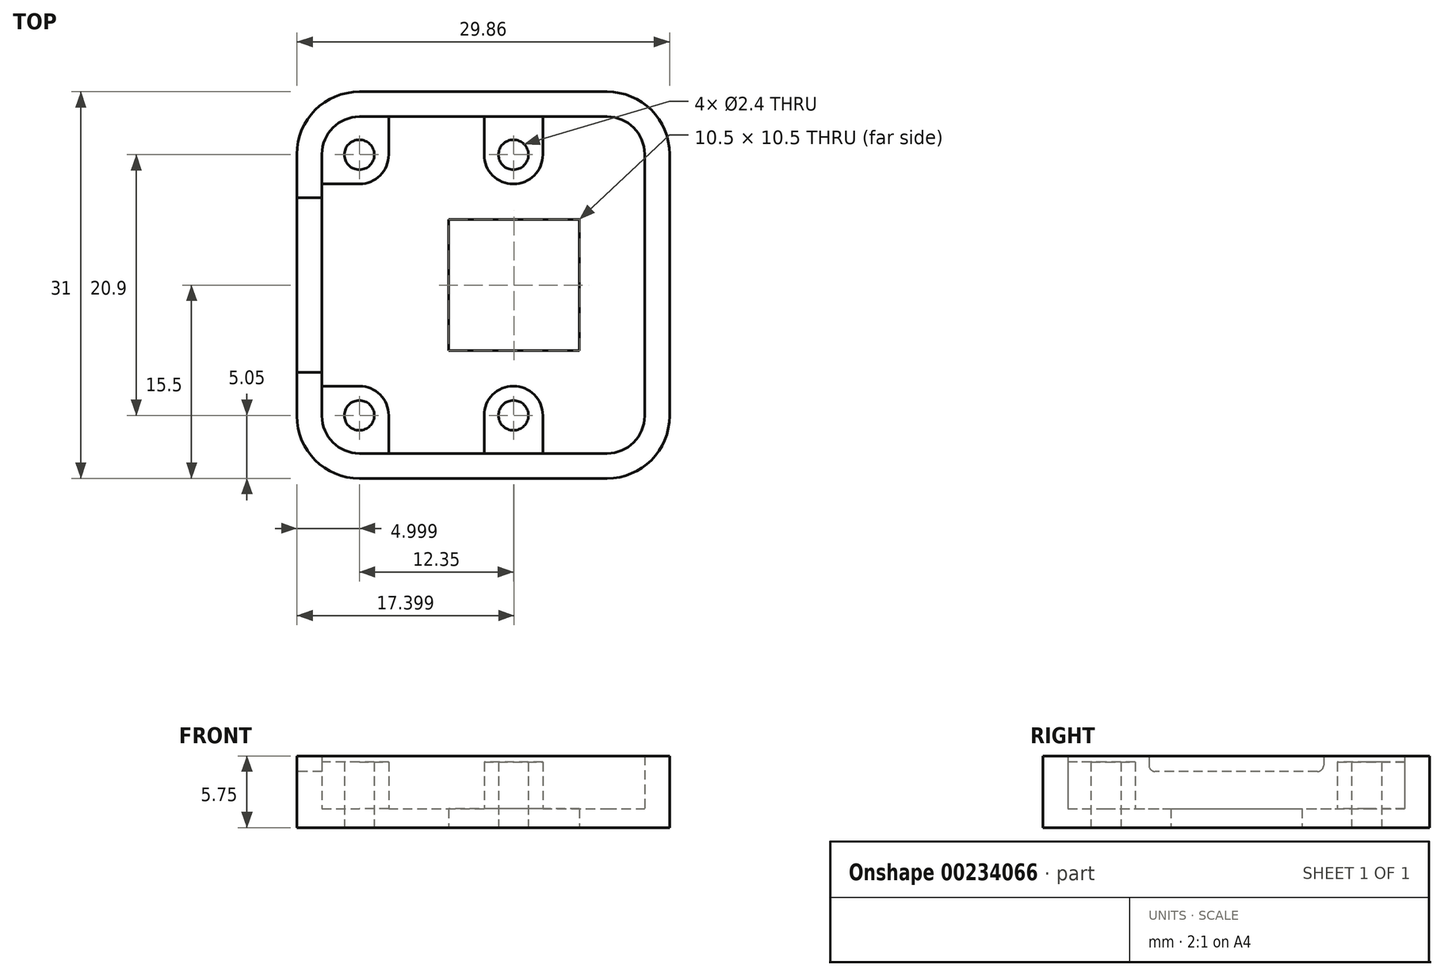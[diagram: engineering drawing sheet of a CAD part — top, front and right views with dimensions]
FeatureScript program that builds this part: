
annotation { "Feature Type Name" : "Feature", "Feature Type Description" : "" }
export const myFeature = defineFeature(function(context is Context, id is Id, definition is map)
    precondition{}
    {
        {
            var Q0;
            Q0=qCreatedBy(makeId("Top.planeOp"),FACE);
            var sketch = newSketch(context, id + "F0", { "sketchPlane" : qUnion([Q0])});
            skPoint(sketch, "E0.middle", {"position": v(0, 0) * mm});
            skPoint(sketch, "E1.visualSharp", {"position": v(-11.93, 12.5) * mm});
            skPoint(sketch, "E2.visualSharp", {"position": v(-11.93, -12.5) * mm});
            skPoint(sketch, "E3.visualSharp", {"position": v(11.93, 12.5) * mm});
            skPoint(sketch, "E4.visualSharp", {"position": v(11.93, -12.5) * mm});
            skLineSegment(sketch, "E5", {"start": v(-9.93, 14.98) * mm, "end": v(-9.93, -15.05) * mm, "construction": true});
            skLineSegment(sketch, "E6", {"start": v(-20.4, -10.45) * mm, "end": v(21.47, -10.45) * mm, "construction": true});
            skLineSegment(sketch, "E7", {"start": v(-14.71, 10.45) * mm, "end": v(19.25, 10.45) * mm, "construction": true});
            skCircle(sketch, "E8", {"center": v(-9.93, 10.45) * mm, "radius": 1.2 * mm});
            skCircle(sketch, "E9", {"center": v(-9.93, -10.45) * mm, "radius": 1.2 * mm});
            skLineSegment(sketch, "E10", {"start": v(2.42, 14.76) * mm, "end": v(2.42, -15.1) * mm, "construction": true});
            skCircle(sketch, "E11", {"center": v(2.42, 10.45) * mm, "radius": 1.2 * mm});
            skCircle(sketch, "E12", {"center": v(2.42, -10.45) * mm, "radius": 1.2 * mm});
            skLineSegment(sketch, "E13", {"start": v(2.47, 15.16) * mm, "end": v(2.47, -14.75) * mm, "construction": true});
            skLineSegment(sketch, "E14.bottom", {"start": v(6.72, -4.25) * mm, "end": v(-1.78, -4.25) * mm});
            skLineSegment(sketch, "E14.top", {"start": v(6.72, 4.25) * mm, "end": v(-1.78, 4.25) * mm});
            skLineSegment(sketch, "E14.left", {"start": v(6.72, -4.25) * mm, "end": v(6.72, 4.25) * mm});
            skLineSegment(sketch, "E14.right", {"start": v(-1.78, -4.25) * mm, "end": v(-1.78, 4.25) * mm});
            skPoint(sketch, "E14.middle", {"position": v(2.47, 0) * mm});
            skCircle(sketch, "E15", {"center": v(-9.93, 10.45) * mm, "radius": 2.35 * mm});
            skCircle(sketch, "E16", {"center": v(-9.93, -10.45) * mm, "radius": 2.35 * mm});
            skCircle(sketch, "E17", {"center": v(2.42, -10.45) * mm, "radius": 2.35 * mm});
            skCircle(sketch, "E18", {"center": v(2.42, 10.45) * mm, "radius": 2.35 * mm});
            skLineSegment(sketch, "E19.0", {"start": v(7.72, 5.25) * mm, "end": v(-2.78, 5.25) * mm});
            skLineSegment(sketch, "E19.1", {"start": v(7.72, -5.25) * mm, "end": v(7.72, 5.25) * mm});
            skLineSegment(sketch, "E19.2", {"start": v(7.72, -5.25) * mm, "end": v(-2.78, -5.25) * mm});
            skLineSegment(sketch, "E19.3", {"start": v(-2.78, -5.25) * mm, "end": v(-2.78, 5.25) * mm});
            skLineSegment(sketch, "E20.0", {"start": v(9.93, 13.5) * mm, "end": v(-9.93, 13.5) * mm});
            skArc(sketch, "E20.1", {"start": v(12.93, 10.5) * mm, "mid": v(12.05, 12.62) * mm, "end": v(9.93, 13.5) * mm});
            skArc(sketch, "E20.2", {"start": v(-9.93, 13.5) * mm, "mid": v(-12.05, 12.62) * mm, "end": v(-12.93, 10.5) * mm});
            skLineSegment(sketch, "E20.3", {"start": v(12.93, 10.5) * mm, "end": v(12.93, -10.5) * mm});
            skLineSegment(sketch, "E20.4", {"start": v(-12.93, 10.5) * mm, "end": v(-12.93, -10.5) * mm});
            skArc(sketch, "E20.5", {"start": v(-12.93, -10.5) * mm, "mid": v(-12.05, -12.62) * mm, "end": v(-9.93, -13.5) * mm});
            skLineSegment(sketch, "E20.6", {"start": v(9.93, -13.5) * mm, "end": v(-9.93, -13.5) * mm});
            skArc(sketch, "E20.7", {"start": v(9.93, -13.5) * mm, "mid": v(12.05, -12.62) * mm, "end": v(12.93, -10.5) * mm});
            skArc(sketch, "E21.0", {"start": v(14.93, 10.5) * mm, "mid": v(13.47, 14.04) * mm, "end": v(9.93, 15.5) * mm});
            skLineSegment(sketch, "E21.1", {"start": v(14.93, 10.5) * mm, "end": v(14.93, -10.5) * mm});
            skLineSegment(sketch, "E21.2", {"start": v(9.93, 15.5) * mm, "end": v(-9.93, 15.5) * mm});
            skArc(sketch, "E21.3", {"start": v(9.93, -15.5) * mm, "mid": v(13.47, -14.04) * mm, "end": v(14.93, -10.5) * mm});
            skArc(sketch, "E21.4", {"start": v(-9.93, 15.5) * mm, "mid": v(-13.47, 14.04) * mm, "end": v(-14.93, 10.5) * mm});
            skLineSegment(sketch, "E21.5", {"start": v(-14.93, 10.5) * mm, "end": v(-14.93, -10.5) * mm});
            skArc(sketch, "E21.6", {"start": v(-14.93, -10.5) * mm, "mid": v(-13.47, -14.04) * mm, "end": v(-9.93, -15.5) * mm});
            skLineSegment(sketch, "E21.7", {"start": v(9.93, -15.5) * mm, "end": v(-9.93, -15.5) * mm});
            skLineSegment(sketch, "E22", {"start": v(-9.93, 8.1) * mm, "end": v(-12.93, 8.1) * mm});
            skLineSegment(sketch, "E23", {"start": v(-7.58, 10.45) * mm, "end": v(-7.58, 13.5) * mm});
            skLineSegment(sketch, "E24", {"start": v(0.07, 10.45) * mm, "end": v(0.07, 13.5) * mm});
            skLineSegment(sketch, "E25", {"start": v(4.77, 10.45) * mm, "end": v(4.77, 13.5) * mm});
            skLineSegment(sketch, "E26", {"start": v(0.07, -10.45) * mm, "end": v(0.07, -13.5) * mm});
            skLineSegment(sketch, "E27", {"start": v(4.77, -10.45) * mm, "end": v(4.77, -13.5) * mm});
            skLineSegment(sketch, "E28", {"start": v(-9.93, -8.1) * mm, "end": v(-12.93, -8.1) * mm});
            skLineSegment(sketch, "E29", {"start": v(-7.58, -10.45) * mm, "end": v(-7.58, -13.5) * mm});
            skSolve(sketch);
        }
        {
            var Q0;
            Q0=makeQuery(id+"F0.imprint","IMPRINT",FACE,{"disambiguationData":[TD([[makeQuery(id+"F0.imprint","IMPRINT",EDGE,{"derivedFrom":sQuery(id+"F0.wireOp",EDGE,"E20.0")}),-1.0]])]});
            var Q1;
            Q1=makeQuery(id+"F0.imprint","IMPRINT",FACE,{"disambiguationData":[TD([[makeQuery(id+"F0.imprint","IMPRINT",EDGE,{"derivedFrom":sQuery(id+"F0.wireOp",EDGE,"E0.left")}),-1.0]])]});
            var Q2;
            Q2=makeQuery(id+"F0.imprint","IMPRINT",FACE,{"disambiguationData":[TD([[makeQuery(id+"F0.imprint","IMPRINT",EDGE,{"derivedFrom":sQuery(id+"F0.wireOp",EDGE,"E12")}),-1.0]])]});
            var Q3;
            {var subQ0=sQuery(id+"F0.wireOp",EDGE,"E2.filletArc");Q3=makeQuery(id+"F0.imprint","IMPRINT",FACE,{"disambiguationData":[TD([[makeQuery(id+"F0.imprint","IMPRINT",EDGE,{"derivedFrom":subQ0}),1.0]])]});}
            var Q4;
            Q4=makeQuery(id+"F0.imprint","IMPRINT",FACE,{"disambiguationData":[TD([[makeQuery(id+"F0.imprint","IMPRINT",EDGE,{"derivedFrom":sQuery(id+"F0.wireOp",EDGE,"E0.left")}),1.0]])]});
            var Q5;
            {var subQ0=sQuery(id+"F0.wireOp",EDGE,"E1.filletArc");Q5=makeQuery(id+"F0.imprint","IMPRINT",FACE,{"disambiguationData":[TD([[makeQuery(id+"F0.imprint","IMPRINT",EDGE,{"derivedFrom":subQ0}),1.0]])]});}
            var Q6;
            Q6=makeQuery(id+"F0.imprint","IMPRINT",FACE,{"disambiguationData":[TD([[makeQuery(id+"F0.imprint","IMPRINT",EDGE,{"derivedFrom":sQuery(id+"F0.wireOp",EDGE,"E11")}),-1.0]])]});
            var Q7;
            {var subQ0=sQuery(id+"F0.wireOp",EDGE,"E18");var subQ1=sQuery(id+"F0.wireOp",EDGE,"E0.bottom");var subQ2=makeQuery(id+"F0.imprint","INTERSECT",VERTEX,{"disambiguationData":[OD(0.0)],"derivedFrom":[subQ1,subQ0]});Q7=makeQuery(id+"F0.imprint","IMPRINT",FACE,{"disambiguationData":[TD([[makeQuery(id+"F0.imprint","IMPRINT",EDGE,{"disambiguationData":[TD([[subQ2,-1.0]])],"derivedFrom":subQ1}),-1.0]])]});}
            var Q8;
            {var subQ0=sQuery(id+"F0.wireOp",EDGE,"E1.filletArc");Q8=makeQuery(id+"F0.imprint","IMPRINT",FACE,{"disambiguationData":[TD([[makeQuery(id+"F0.imprint","IMPRINT",EDGE,{"derivedFrom":subQ0}),-1.0]])]});}
            var Q9;
            {var subQ0=sQuery(id+"F0.wireOp",EDGE,"E2.filletArc");Q9=makeQuery(id+"F0.imprint","IMPRINT",FACE,{"disambiguationData":[TD([[makeQuery(id+"F0.imprint","IMPRINT",EDGE,{"derivedFrom":subQ0}),-1.0]])]});}
            var Q10;
            {var subQ0=sQuery(id+"F0.wireOp",EDGE,"E17");var subQ1=sQuery(id+"F0.wireOp",EDGE,"E0.top");var subQ2=makeQuery(id+"F0.imprint","INTERSECT",VERTEX,{"disambiguationData":[OD(0.0)],"derivedFrom":[subQ1,subQ0]});Q10=makeQuery(id+"F0.imprint","IMPRINT",FACE,{"disambiguationData":[TD([[makeQuery(id+"F0.imprint","IMPRINT",EDGE,{"disambiguationData":[TD([[subQ2,-1.0]])],"derivedFrom":subQ1}),1.0]])]});}
            var Q11;
            {var subQ0=sQuery(id+"F0.wireOp",EDGE,"E20.2");Q11=makeQuery(id+"F0.imprint","IMPRINT",FACE,{"disambiguationData":[TD([[makeQuery(id+"F0.imprint","IMPRINT",EDGE,{"derivedFrom":subQ0}),1.0]])]});}
            var Q12;
            {var subQ0=sQuery(id+"F0.wireOp",EDGE,"E22");var subQ1=sQuery(id+"F0.wireOp",EDGE,"E0.right");var subQ2=makeQuery(id+"F0.imprint","INTERSECT",VERTEX,{"derivedFrom":[subQ1,subQ0]});Q12=makeQuery(id+"F0.imprint","IMPRINT",FACE,{"disambiguationData":[TD([[makeQuery(id+"F0.imprint","IMPRINT",EDGE,{"disambiguationData":[TD([[subQ2,-1.0]])],"derivedFrom":subQ1}),-1.0]])]});}
            var Q13;
            {var subQ0=sQuery(id+"F0.wireOp",EDGE,"E20.5");Q13=makeQuery(id+"F0.imprint","IMPRINT",FACE,{"disambiguationData":[TD([[makeQuery(id+"F0.imprint","IMPRINT",EDGE,{"derivedFrom":subQ0}),1.0]])]});}
            var Q14;
            {var subQ0=sQuery(id+"F0.wireOp",EDGE,"E28");var subQ1=sQuery(id+"F0.wireOp",EDGE,"E0.right");var subQ2=makeQuery(id+"F0.imprint","INTERSECT",VERTEX,{"derivedFrom":[subQ1,subQ0]});Q14=makeQuery(id+"F0.imprint","IMPRINT",FACE,{"disambiguationData":[TD([[makeQuery(id+"F0.imprint","IMPRINT",EDGE,{"disambiguationData":[TD([[subQ2,-1.0]])],"derivedFrom":subQ1}),1.0]])]});}
            var Q15;
            {var subQ0=sQuery(id+"F0.wireOp",EDGE,"E29");var subQ1=sQuery(id+"F0.wireOp",EDGE,"E0.top");var subQ2=makeQuery(id+"F0.imprint","INTERSECT",VERTEX,{"derivedFrom":[subQ1,subQ0]});Q15=makeQuery(id+"F0.imprint","IMPRINT",FACE,{"disambiguationData":[TD([[makeQuery(id+"F0.imprint","IMPRINT",EDGE,{"disambiguationData":[TD([[subQ2,-1.0]])],"derivedFrom":subQ1}),-1.0]])]});}
            var Q16;
            {var subQ0=sQuery(id+"F0.wireOp",EDGE,"E26");var subQ1=sQuery(id+"F0.wireOp",EDGE,"E0.top");var subQ2=makeQuery(id+"F0.imprint","INTERSECT",VERTEX,{"derivedFrom":[subQ1,subQ0]});Q16=makeQuery(id+"F0.imprint","IMPRINT",FACE,{"disambiguationData":[TD([[makeQuery(id+"F0.imprint","IMPRINT",EDGE,{"disambiguationData":[TD([[subQ2,-1.0]])],"derivedFrom":subQ1}),1.0]])]});}
            var Q17;
            {var subQ3=sQuery(id+"F0.wireOp",EDGE,"E27");var subQ6=sQuery(id+"F0.wireOp",EDGE,"E0.top");var subQ10=makeQuery(id+"F0.imprint","INTERSECT",VERTEX,{"derivedFrom":[subQ6,subQ3]});Q17=makeQuery(id+"F0.imprint","IMPRINT",FACE,{"disambiguationData":[TD([[makeQuery(id+"F0.imprint","IMPRINT",EDGE,{"disambiguationData":[TD([[subQ10,-1.0]])],"derivedFrom":subQ6}),1.0]])]});}
            var Q18;
            {var subQ0=sQuery(id+"F0.wireOp",EDGE,"E27");var subQ1=sQuery(id+"F0.wireOp",EDGE,"E0.top");var subQ2=makeQuery(id+"F0.imprint","INTERSECT",VERTEX,{"derivedFrom":[subQ1,subQ0]});Q18=makeQuery(id+"F0.imprint","IMPRINT",FACE,{"disambiguationData":[TD([[makeQuery(id+"F0.imprint","IMPRINT",EDGE,{"disambiguationData":[TD([[subQ2,-1.0]])],"derivedFrom":subQ1}),-1.0]])]});}
            var Q19;
            {var subQ0=sQuery(id+"F0.wireOp",EDGE,"E17");var subQ1=sQuery(id+"F0.wireOp",EDGE,"E0.top");var subQ2=makeQuery(id+"F0.imprint","INTERSECT",VERTEX,{"disambiguationData":[OD(1.0)],"derivedFrom":[subQ1,subQ0]});Q19=makeQuery(id+"F0.imprint","IMPRINT",FACE,{"disambiguationData":[TD([[makeQuery(id+"F0.imprint","IMPRINT",EDGE,{"disambiguationData":[TD([[subQ2,-1.0]])],"derivedFrom":subQ1}),-1.0]])]});}
            var Q20;
            {var subQ0=sQuery(id+"F0.wireOp",EDGE,"E23");var subQ1=sQuery(id+"F0.wireOp",EDGE,"E0.bottom");var subQ2=makeQuery(id+"F0.imprint","INTERSECT",VERTEX,{"derivedFrom":[subQ1,subQ0]});Q20=makeQuery(id+"F0.imprint","IMPRINT",FACE,{"disambiguationData":[TD([[makeQuery(id+"F0.imprint","IMPRINT",EDGE,{"disambiguationData":[TD([[subQ2,-1.0]])],"derivedFrom":subQ1}),1.0]])]});}
            var Q21;
            {var subQ0=sQuery(id+"F0.wireOp",EDGE,"E15");var subQ1=sQuery(id+"F0.wireOp",EDGE,"E0.right");var subQ2=makeQuery(id+"F0.imprint","INTERSECT",VERTEX,{"derivedFrom":[subQ1,subQ0]});Q21=makeQuery(id+"F0.imprint","IMPRINT",FACE,{"disambiguationData":[TD([[makeQuery(id+"F0.imprint","IMPRINT",EDGE,{"disambiguationData":[TD([[subQ2,-1.0]])],"derivedFrom":subQ1}),1.0]])]});}
            var Q22;
            {var subQ0=sQuery(id+"F0.wireOp",EDGE,"E24");var subQ1=sQuery(id+"F0.wireOp",EDGE,"E0.bottom");var subQ2=makeQuery(id+"F0.imprint","INTERSECT",VERTEX,{"derivedFrom":[subQ1,subQ0]});Q22=makeQuery(id+"F0.imprint","IMPRINT",FACE,{"disambiguationData":[TD([[makeQuery(id+"F0.imprint","IMPRINT",EDGE,{"disambiguationData":[TD([[subQ2,-1.0]])],"derivedFrom":subQ1}),-1.0]])]});}
            var Q23;
            {var subQ0=sQuery(id+"F0.wireOp",EDGE,"E18");var subQ1=sQuery(id+"F0.wireOp",EDGE,"E0.bottom");var subQ2=makeQuery(id+"F0.imprint","INTERSECT",VERTEX,{"disambiguationData":[OD(1.0)],"derivedFrom":[subQ1,subQ0]});Q23=makeQuery(id+"F0.imprint","IMPRINT",FACE,{"disambiguationData":[TD([[makeQuery(id+"F0.imprint","IMPRINT",EDGE,{"disambiguationData":[TD([[subQ2,-1.0]])],"derivedFrom":subQ1}),1.0]])]});}
            var Q24;
            {var subQ1=sQuery(id+"F0.wireOp",EDGE,"E0.bottom");var subQ7=sQuery(id+"F0.wireOp",EDGE,"E25");var subQ9=makeQuery(id+"F0.imprint","INTERSECT",VERTEX,{"derivedFrom":[subQ1,subQ7]});Q24=makeQuery(id+"F0.imprint","IMPRINT",FACE,{"disambiguationData":[TD([[makeQuery(id+"F0.imprint","IMPRINT",EDGE,{"disambiguationData":[TD([[subQ9,-1.0]])],"derivedFrom":subQ1}),-1.0]])]});}
            var Q25;
            {var subQ0=sQuery(id+"F0.wireOp",EDGE,"E25");var subQ1=sQuery(id+"F0.wireOp",EDGE,"E0.bottom");var subQ2=makeQuery(id+"F0.imprint","INTERSECT",VERTEX,{"derivedFrom":[subQ1,subQ0]});Q25=makeQuery(id+"F0.imprint","IMPRINT",FACE,{"disambiguationData":[TD([[makeQuery(id+"F0.imprint","IMPRINT",EDGE,{"disambiguationData":[TD([[subQ2,-1.0]])],"derivedFrom":subQ1}),1.0]])]});}
            var Q26;
            Q26=makeQuery(id+"F0.imprint","IMPRINT",FACE,{"disambiguationData":[TD([[makeQuery(id+"F0.imprint","IMPRINT",EDGE,{"derivedFrom":sQuery(id+"F0.wireOp",EDGE,"E19.0")}),-1.0]])]});
            var Q27;
            Q27=makeQuery(id+"F0.imprint","IMPRINT",FACE,{"disambiguationData":[TD([[makeQuery(id+"F0.imprint","IMPRINT",EDGE,{"derivedFrom":sQuery(id+"F0.wireOp",EDGE,"E9")}),-1.0]])]});
            var Q28;
            {var subQ0=sQuery(id+"F0.wireOp",EDGE,"E26");Q28=makeQuery(id+"F0.imprint","IMPRINT",FACE,{"disambiguationData":[TD([[makeQuery(id+"F0.imprint","IMPRINT",EDGE,{"derivedFrom":subQ0}),1.0]])]});}
            var Q29;
            Q29=makeQuery(id+"F0.imprint","IMPRINT",FACE,{"disambiguationData":[TD([[makeQuery(id+"F0.imprint","IMPRINT",EDGE,{"derivedFrom":sQuery(id+"F0.wireOp",EDGE,"E8")}),-1.0]])]});
            var Q30;
            {var subQ0=sQuery(id+"F0.wireOp",EDGE,"E24");Q30=makeQuery(id+"F0.imprint","IMPRINT",FACE,{"disambiguationData":[TD([[makeQuery(id+"F0.imprint","IMPRINT",EDGE,{"derivedFrom":subQ0}),-1.0]])]});}
            extrude(context, id + "F1", {"entities" : qUnion([Q0, Q1, Q2, Q3, Q4, Q5, Q6, Q7, Q8, Q9, Q10, Q11, Q12, Q13, Q14, Q15, Q16, Q17, Q18, Q19, Q20, Q21, Q22, Q23, Q24, Q25, Q26, Q27, Q28, Q29, Q30]), "depth" : 1.5 * mm});
        }
        {
            var Q0;
            {var subQ1=sQuery(id+"F0.wireOp",EDGE,"E20.2");Q0=makeQuery(id+"F0.imprint","IMPRINT",FACE,{"disambiguationData":[TD([[makeQuery(id+"F0.imprint","IMPRINT",EDGE,{"derivedFrom":subQ1}),1.0]])]});}
            var Q1;
            Q1=makeQuery(id+"F0.imprint","IMPRINT",FACE,{"disambiguationData":[TD([[makeQuery(id+"F0.imprint","IMPRINT",EDGE,{"derivedFrom":sQuery(id+"F0.wireOp",EDGE,"E8")}),-1.0]])]});
            var Q2;
            Q2=makeQuery(id+"F0.imprint","IMPRINT",FACE,{"disambiguationData":[TD([[makeQuery(id+"F0.imprint","IMPRINT",EDGE,{"derivedFrom":sQuery(id+"F0.wireOp",EDGE,"E11")}),-1.0]])]});
            var Q3;
            {var subQ0=sQuery(id+"F0.wireOp",EDGE,"E24");Q3=makeQuery(id+"F0.imprint","IMPRINT",FACE,{"disambiguationData":[TD([[makeQuery(id+"F0.imprint","IMPRINT",EDGE,{"derivedFrom":subQ0}),-1.0]])]});}
            var Q4;
            Q4=makeQuery(id+"F0.imprint","IMPRINT",FACE,{"disambiguationData":[TD([[makeQuery(id+"F0.imprint","IMPRINT",EDGE,{"derivedFrom":sQuery(id+"F0.wireOp",EDGE,"E12")}),-1.0]])]});
            var Q5;
            {var subQ0=sQuery(id+"F0.wireOp",EDGE,"E26");Q5=makeQuery(id+"F0.imprint","IMPRINT",FACE,{"disambiguationData":[TD([[makeQuery(id+"F0.imprint","IMPRINT",EDGE,{"derivedFrom":subQ0}),1.0]])]});}
            var Q6;
            Q6=makeQuery(id+"F0.imprint","IMPRINT",FACE,{"disambiguationData":[TD([[makeQuery(id+"F0.imprint","IMPRINT",EDGE,{"derivedFrom":sQuery(id+"F0.wireOp",EDGE,"E9")}),-1.0]])]});
            var Q7;
            {var subQ1=sQuery(id+"F0.wireOp",EDGE,"E20.5");Q7=makeQuery(id+"F0.imprint","IMPRINT",FACE,{"disambiguationData":[TD([[makeQuery(id+"F0.imprint","IMPRINT",EDGE,{"derivedFrom":subQ1}),1.0]])]});}
            extrude(context, id + "F2", {"entities" : qUnion([Q0, Q1, Q2, Q3, Q4, Q5, Q6, Q7]), "operationType" : NewBodyOperationType.ADD, "depth" : 5.25 * mm});
        }
        {
            var Q0;
            {var subQ12=sQuery(id+"F0.wireOp",EDGE,"E20.1");Q0=makeQuery(id+"F0.imprint","IMPRINT",FACE,{"disambiguationData":[TD([[makeQuery(id+"F0.imprint","IMPRINT",EDGE,{"derivedFrom":subQ12}),-1.0]])]});}
            extrude(context, id + "F3", {"entities" : qUnion([Q0]), "operationType" : NewBodyOperationType.ADD, "depth" : 5.75 * mm});
        }
        {
            var Q0;
            {var subQ0=sQuery(id+"F0.wireOp",EDGE,"E21.5");Q0=makeQuery(id+"F3.boolean.opBoolean","MERGE",FACE,{"derivedFrom":[makeQuery(id+"F1.opExtrude","SWEPT_FACE",FACE,{"disambiguationData":[OSD([subQ0])]}),makeQuery(id+"F3.opExtrude","SWEPT_FACE",FACE,{"disambiguationData":[OSD([subQ0])]})]});}
            var sketch = newSketch(context, id + "F4", { "sketchPlane" : qUnion([Q0])});
            skLineSegment(sketch, "E30.bottom", {"start": v(-7, 5.75) * mm, "end": v(7, 5.75) * mm});
            skLineSegment(sketch, "E30.top", {"start": v(-6.5, 4.5) * mm, "end": v(6.5, 4.5) * mm});
            skLineSegment(sketch, "E30.left", {"start": v(-7, 5.75) * mm, "end": v(-7, 5) * mm});
            skLineSegment(sketch, "E30.right", {"start": v(7, 5.75) * mm, "end": v(7, 5) * mm});
            skPoint(sketch, "E31.visualSharp", {"position": v(-7, 4.5) * mm});
            skArc(sketch, "E31.filletArc", {"start": v(-7, 5) * mm, "mid": v(-6.85, 4.65) * mm, "end": v(-6.5, 4.5) * mm});
            skPoint(sketch, "E32.visualSharp", {"position": v(7, 4.5) * mm});
            skArc(sketch, "E32.filletArc", {"start": v(6.5, 4.5) * mm, "mid": v(6.85, 4.65) * mm, "end": v(7, 5) * mm});
            skSolve(sketch);
        }
        {
            var Q0;
            Q0=makeQuery(id+"F4.imprint","IMPRINT",FACE,{"disambiguationData":[TD([[makeQuery(id+"F4.imprint","IMPRINT",EDGE,{"derivedFrom":sQuery(id+"F4.wireOp",EDGE,"E30.bottom")}),-1.0]])]});
            extrude(context, id + "F5", {"entities" : qUnion([Q0]), "operationType" : NewBodyOperationType.REMOVE, "oppositeDirection" : true, "depth" : 2 * mm});
        }
    });
